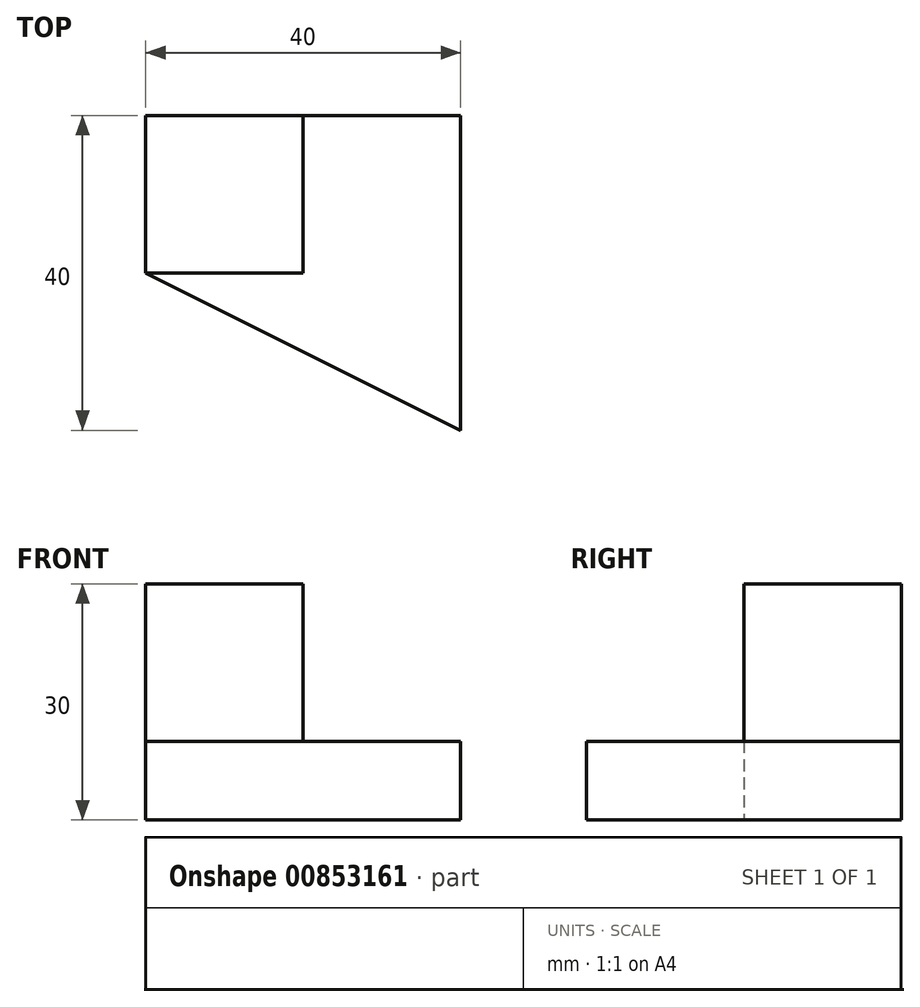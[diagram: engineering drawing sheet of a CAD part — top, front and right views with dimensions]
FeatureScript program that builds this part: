
annotation { "Feature Type Name" : "Feature", "Feature Type Description" : "" }
export const myFeature = defineFeature(function(context is Context, id is Id, definition is map)
    precondition{}
    {
        {
            var Q0;
            Q0=qCreatedBy(makeId("Top.planeOp"),FACE);
            var sketch = newSketch(context, id + "F0", { "sketchPlane" : qUnion([Q0])});
            skLineSegment(sketch, "E0.bottom", {"start": v(-46.13, 28.7) * mm, "end": v(-26.13, 28.7) * mm});
            skLineSegment(sketch, "E0.top", {"start": v(-46.13, 8.7) * mm, "end": v(-26.13, 8.7) * mm});
            skLineSegment(sketch, "E0.left", {"start": v(-46.13, 28.7) * mm, "end": v(-46.13, 8.7) * mm});
            skLineSegment(sketch, "E0.right", {"start": v(-26.13, 28.7) * mm, "end": v(-26.13, 8.7) * mm});
            skLineSegment(sketch, "E1", {"start": v(-6.13, 28.7) * mm, "end": v(-6.13, -11.3) * mm});
            skLineSegment(sketch, "E2", {"start": v(-46.13, 28.7) * mm, "end": v(-6.13, 28.7) * mm});
            skLineSegment(sketch, "E3", {"start": v(-46.13, 8.7) * mm, "end": v(-6.13, -11.3) * mm});
            skSolve(sketch);
        }
        {
            var Q0;
            Q0=makeQuery(id+"F0.imprint","IMPRINT",FACE,{"disambiguationData":[TD([[makeQuery(id+"F0.imprint","IMPRINT",EDGE,{"derivedFrom":sQuery(id+"F0.wireOp",EDGE,"E0.top")}),-1.0]])]});
            extrude(context, id + "F1", {"entities" : qUnion([Q0]), "depth" : 10 * mm, "offsetDistance" : 25 * mm});
        }
        {
            var Q0;
            Q0=makeQuery(id+"F0.imprint","IMPRINT",FACE,{"disambiguationData":[TD([[makeQuery(id+"F0.imprint","IMPRINT",EDGE,{"derivedFrom":sQuery(id+"F0.wireOp",EDGE,"E0.top")}),1.0]])]});
            extrude(context, id + "F2", {"entities" : qUnion([Q0]), "operationType" : NewBodyOperationType.ADD, "depth" : 30 * mm, "offsetDistance" : 25 * mm});
        }
    });
